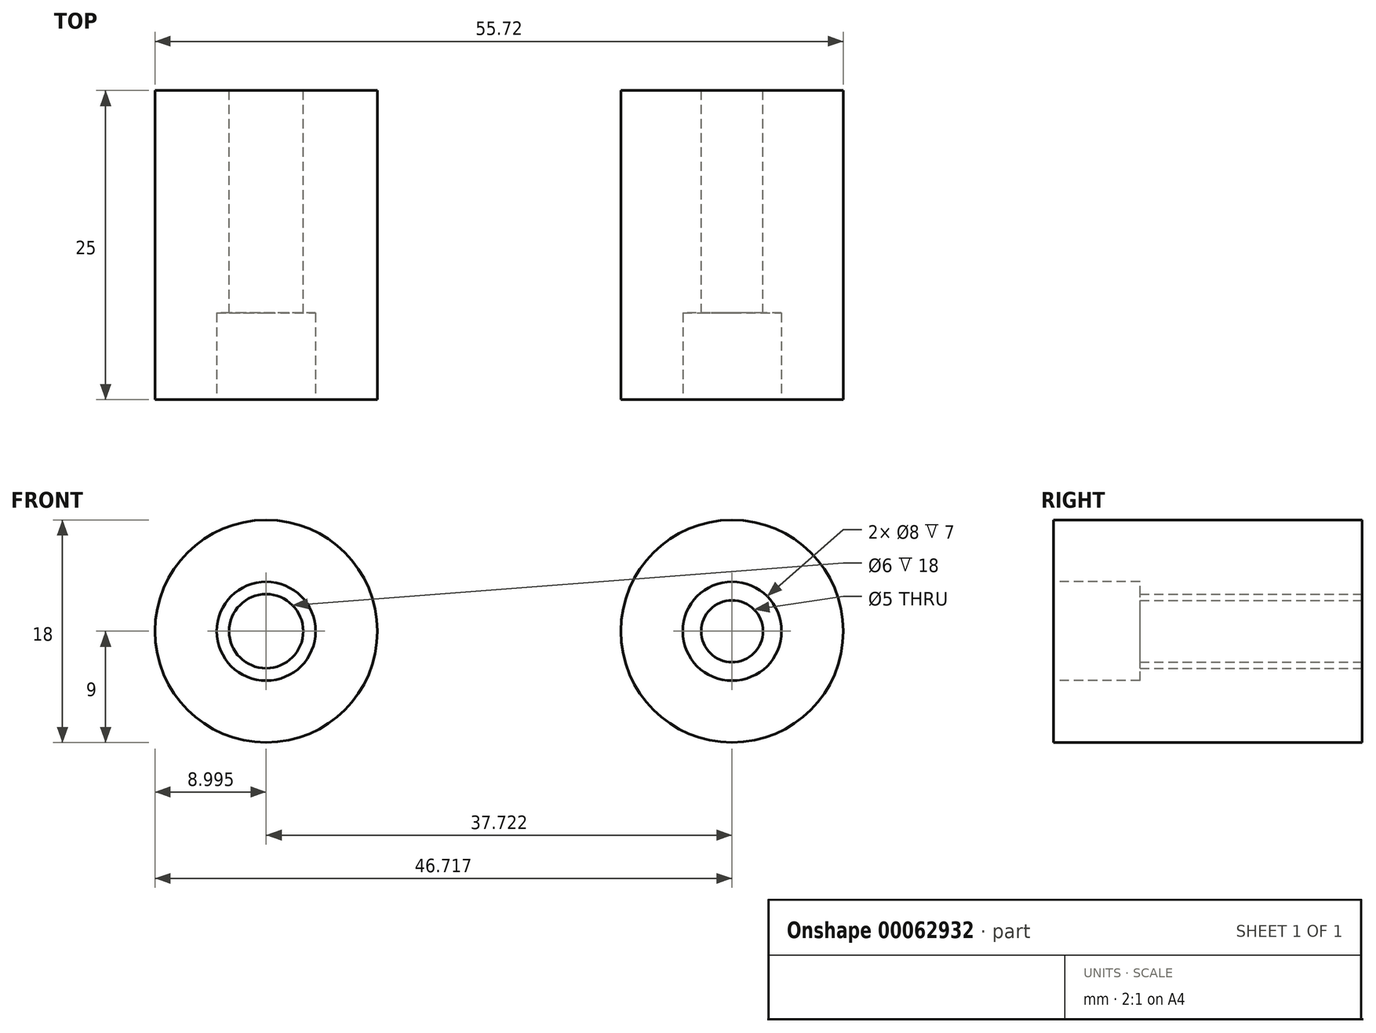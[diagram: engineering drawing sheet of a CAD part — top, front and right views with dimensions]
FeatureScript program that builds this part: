
annotation { "Feature Type Name" : "Feature", "Feature Type Description" : "" }
export const myFeature = defineFeature(function(context is Context, id is Id, definition is map)
    precondition{}
    {
        {
            var Q0;
            Q0=qCreatedBy(makeId("Front.planeOp"),FACE);
            var sketch = newSketch(context, id + "F0", { "sketchPlane" : qUnion([Q0])});
            skCircle(sketch, "E0", {"center": v(-19.53, 0) * mm, "radius": 9 * mm});
            skCircle(sketch, "E1", {"center": v(18.19, 0) * mm, "radius": 9 * mm});
            skCircle(sketch, "E2", {"center": v(-19.53, 0) * mm, "radius": 3 * mm});
            skCircle(sketch, "E3", {"center": v(18.19, 0) * mm, "radius": 2.5 * mm});
            skSolve(sketch);
        }
        {
            var Q0;
            Q0 = qSketchRegion(id + "F0", true);
            extrude(context, id + "F1", {"entities" : qUnion([Q0]), "depth" : 25 * mm});
        }
        {
            var Q0;
            Q0=makeQuery(id+"F1.opExtrude","CAP_FACE",FACE,{"disambiguationData":[OSD([sQuery(id+"F0.wireOp",EDGE,"E0"),sQuery(id+"F0.wireOp",EDGE,"E2")])],"isStart":false});
            var sketch = newSketch(context, id + "F2", { "sketchPlane" : qUnion([Q0])});
            skCircle(sketch, "E4", {"center": v(-19.53, 0) * mm, "radius": 4 * mm});
            skSolve(sketch);
        }
        {
            var Q0;
            Q0 = qSketchRegion(id + "F2", true);
            extrude(context, id + "F3", {"entities" : qUnion([Q0]), "operationType" : NewBodyOperationType.REMOVE, "oppositeDirection" : true, "depth" : 7 * mm});
        }
        {
            var Q0;
            Q0=makeQuery(id+"F1.opExtrude","CAP_FACE",FACE,{"disambiguationData":[OSD([sQuery(id+"F0.wireOp",EDGE,"E1"),sQuery(id+"F0.wireOp",EDGE,"E3")])],"isStart":false});
            var sketch = newSketch(context, id + "F4", { "sketchPlane" : qUnion([Q0])});
            skCircle(sketch, "E5", {"center": v(18.19, 0) * mm, "radius": 4 * mm});
            skSolve(sketch);
        }
        {
            var Q0;
            Q0 = qSketchRegion(id + "F4", true);
            extrude(context, id + "F5", {"entities" : qUnion([Q0]), "operationType" : NewBodyOperationType.REMOVE, "oppositeDirection" : true, "depth" : 7 * mm});
        }
    });
